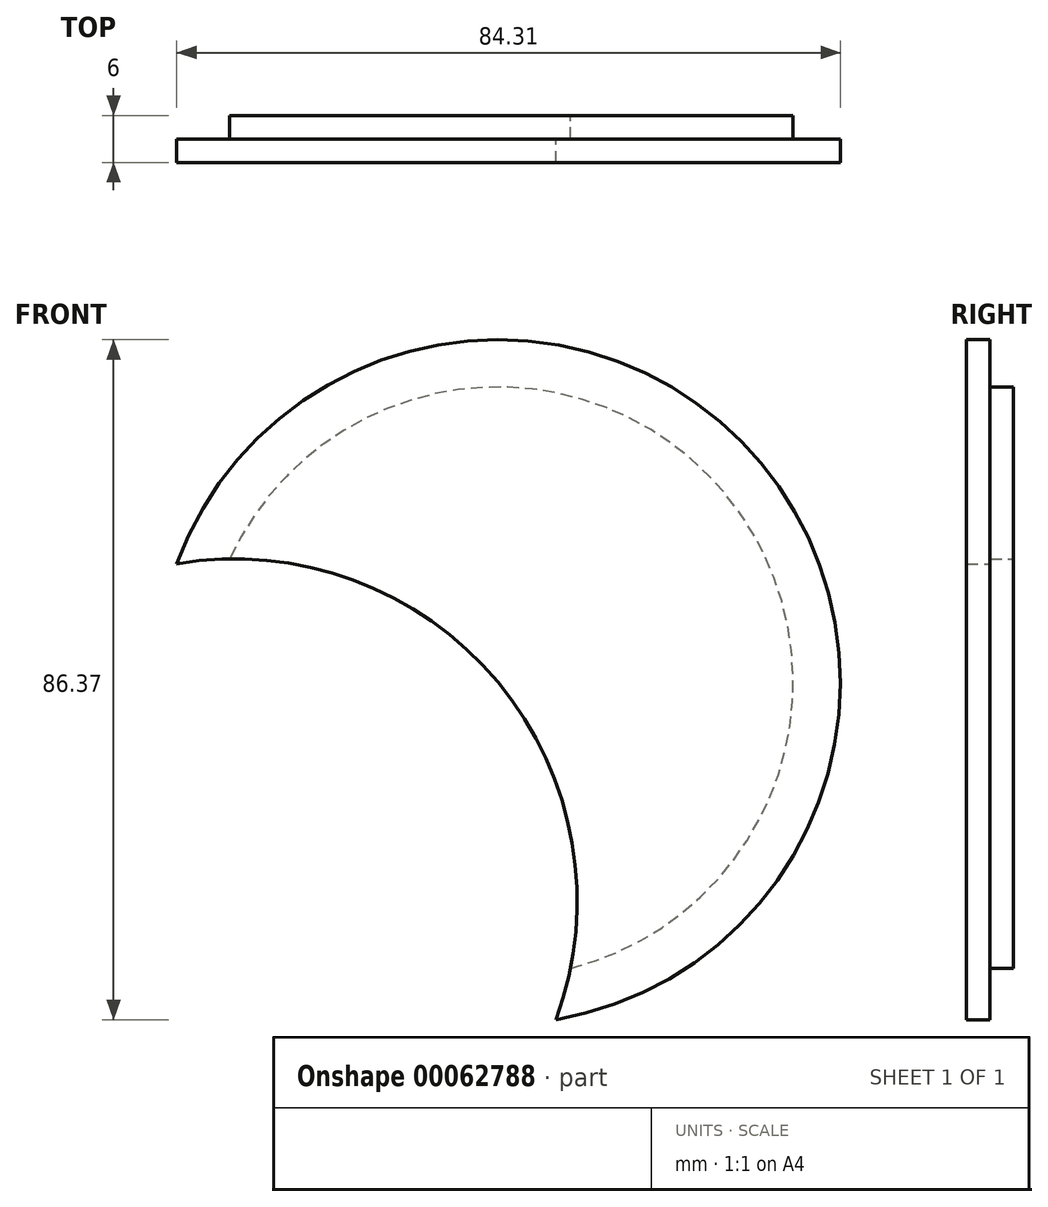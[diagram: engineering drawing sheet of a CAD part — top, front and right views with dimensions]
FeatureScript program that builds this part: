
annotation { "Feature Type Name" : "Feature", "Feature Type Description" : "" }
export const myFeature = defineFeature(function(context is Context, id is Id, definition is map)
    precondition{}
    {
        {
            var Q0;
            Q0=qCreatedBy(makeId("Front.planeOp"),FACE);
            var sketch = newSketch(context, id + "F0", { "sketchPlane" : qUnion([Q0])});
            skCircle(sketch, "E0", {"center": v(0, 0) * mm, "radius": 37.5 * mm});
            skSolve(sketch);
        }
        {
            var Q0;
            Q0=qSketchRegion(id+"F0",true);
            extrude(context, id + "F1", {"entities" : qUnion([Q0]), "depth" : 3 * mm});
        }
        {
            var Q0;
            Q0=makeQuery(id+"F1.opExtrude","CAP_FACE",FACE,{"disambiguationData":[OSD([sQuery(id+"F0.wireOp",EDGE,"E0")])],"isStart":false});
            var sketch = newSketch(context, id + "F2", { "sketchPlane" : qUnion([Q0])});
            skCircle(sketch, "E1.0", {"center": v(0, 0) * mm, "radius": 43.5 * mm});
            skSolve(sketch);
        }
        {
            var Q0;
            Q0=qSketchRegion(id+"F2",true);
            extrude(context, id + "F3", {"entities" : qUnion([Q0]), "operationType" : NewBodyOperationType.ADD, "depth" : 3 * mm});
        }
        {
            var Q0;
            Q0=makeQuery(id+"F1.opExtrude","CAP_FACE",FACE,{"disambiguationData":[OSD([sQuery(id+"F0.wireOp",EDGE,"E0")])],"isStart":true});
            var sketch = newSketch(context, id + "F4", { "sketchPlane" : qUnion([Q0])});
            skArc(sketch, "E2.0", {"start": v(-7.38, -42.87) * mm, "mid": v(33.44, -27.82) * mm, "end": v(40.81, 15.05) * mm});
            skArc(sketch, "E3", {"start": v(40.81, 15.05) * mm, "mid": v(0, 0) * mm, "end": v(-7.38, -42.87) * mm});
            skSolve(sketch);
        }
        {
            var Q0;
            Q0 = qSketchRegion(id + "F4", true);
            var Q1;
            Q1 = qConstructionFilter(qBodyType(qCreatedBy(id + "F4" ,EDGE), BodyType.WIRE), ConstructionObject.NO);
            extrude(context, id + "F5", {"entities" : qUnion([Q0]), "operationType" : NewBodyOperationType.REMOVE, "surfaceEntities" : qUnion([Q1]), "oppositeDirection" : true, "depth" : 25 * mm});
        }
    });
